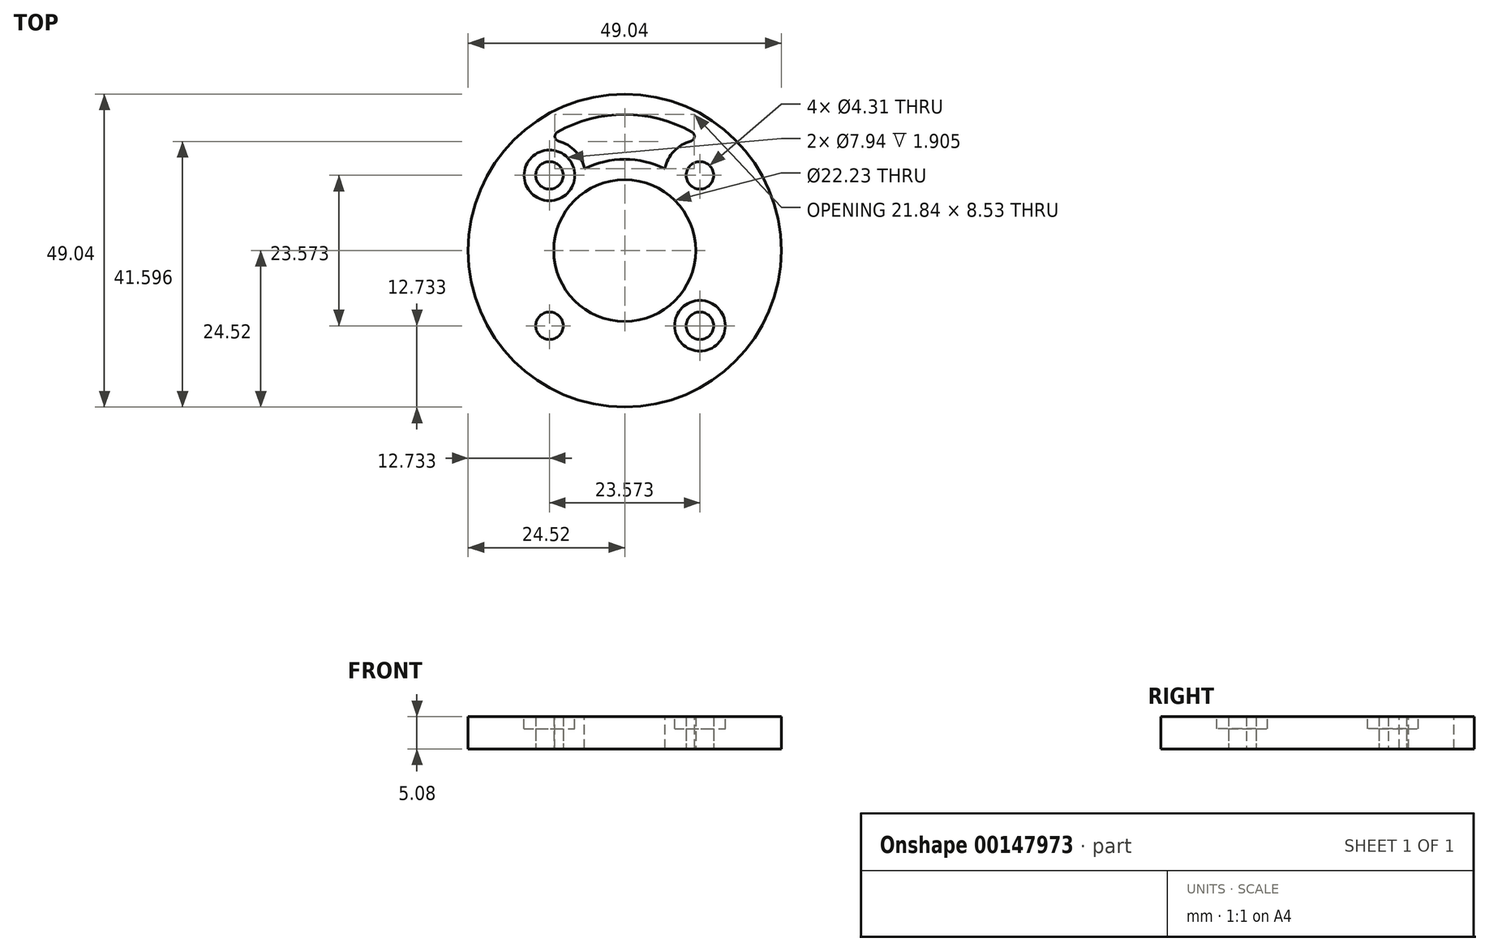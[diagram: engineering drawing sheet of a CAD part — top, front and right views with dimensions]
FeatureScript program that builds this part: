
annotation { "Feature Type Name" : "Feature", "Feature Type Description" : "" }
export const myFeature = defineFeature(function(context is Context, id is Id, definition is map)
    precondition{}
    {
        {
            var Q0;
            Q0=qCreatedBy(makeId("Top.planeOp"),FACE);
            var sketch = newSketch(context, id + "F0", { "sketchPlane" : qUnion([Q0])});
            skCircle(sketch, "E0", {"center": v(0, 0) * mm, "radius": 24.52 * mm});
            skCircle(sketch, "E1", {"center": v(0, 0) * mm, "radius": 11.11 * mm});
            skLineSegment(sketch, "E2.bottom", {"start": v(-11.79, 11.79) * mm, "end": v(11.79, 11.79) * mm, "construction": true});
            skLineSegment(sketch, "E2.top", {"start": v(-11.79, -11.79) * mm, "end": v(11.79, -11.79) * mm, "construction": true});
            skLineSegment(sketch, "E2.left", {"start": v(-11.79, 11.79) * mm, "end": v(-11.79, -11.79) * mm, "construction": true});
            skLineSegment(sketch, "E2.right", {"start": v(11.79, 11.79) * mm, "end": v(11.79, -11.79) * mm, "construction": true});
            skCircle(sketch, "E3", {"center": v(11.79, 11.79) * mm, "radius": 2.15 * mm});
            skCircle(sketch, "E4", {"center": v(-11.79, 11.79) * mm, "radius": 2.15 * mm});
            skCircle(sketch, "E5", {"center": v(-11.79, -11.79) * mm, "radius": 2.15 * mm});
            skCircle(sketch, "E6", {"center": v(11.79, -11.79) * mm, "radius": 2.15 * mm});
            skCircle(sketch, "E7", {"center": v(-11.79, -11.79) * mm, "radius": 3.97 * mm, "construction": true});
            skCircle(sketch, "E8", {"center": v(11.79, 11.79) * mm, "radius": 3.97 * mm, "construction": true});
            skSolve(sketch);
        }
        {
            var Q0;
            Q0=qSketchRegion(id+"F0",true);
            extrude(context, id + "F1", {"entities" : qUnion([Q0]), "depth" : 5.08 * mm});
        }
        {
            var Q0;
            Q0=makeQuery(id+"F1.opExtrude","CAP_FACE",FACE,{"disambiguationData":[OSD([sQuery(id+"F0.wireOp",EDGE,"E0"),sQuery(id+"F0.wireOp",EDGE,"E1"),sQuery(id+"F0.wireOp",EDGE,"E3"),sQuery(id+"F0.wireOp",EDGE,"E4"),sQuery(id+"F0.wireOp",EDGE,"E5"),sQuery(id+"F0.wireOp",EDGE,"E6")])],"isStart":false});
            var sketch = newSketch(context, id + "F2", { "sketchPlane" : qUnion([Q0])});
            skArc(sketch, "E9", {"start": v(-6.55, 9.92) * mm, "mid": v(-7.46, 15.27) * mm, "end": v(-12.5, 17.3) * mm});
            skArc(sketch, "E10", {"start": v(12.5, 17.3) * mm, "mid": v(7.46, 15.27) * mm, "end": v(6.55, 9.92) * mm});
            skArc(sketch, "E11", {"start": v(12.5, 17.3) * mm, "mid": v(0, 21.34) * mm, "end": v(-12.5, 17.3) * mm});
            skArc(sketch, "E12", {"start": v(8.28, 11.65) * mm, "mid": v(0, 14.29) * mm, "end": v(-8.28, 11.65) * mm});
            skLineSegment(sketch, "E13.bottom", {"start": v(-9.92, 6.55) * mm, "end": v(-6.55, 9.92) * mm, "construction": true});
            skLineSegment(sketch, "E13.top", {"start": v(-11.65, 8.28) * mm, "end": v(-8.28, 11.65) * mm, "construction": true});
            skLineSegment(sketch, "E13.left", {"start": v(-11.65, 8.28) * mm, "end": v(-9.92, 6.55) * mm, "construction": true});
            skLineSegment(sketch, "E13.right", {"start": v(-8.28, 11.65) * mm, "end": v(-6.55, 9.92) * mm});
            skLineSegment(sketch, "E14.bottom", {"start": v(9.92, 6.55) * mm, "end": v(6.55, 9.92) * mm, "construction": true});
            skLineSegment(sketch, "E14.top", {"start": v(11.65, 8.28) * mm, "end": v(8.28, 11.65) * mm, "construction": true});
            skLineSegment(sketch, "E14.left", {"start": v(11.65, 8.28) * mm, "end": v(9.92, 6.55) * mm, "construction": true});
            skLineSegment(sketch, "E14.right", {"start": v(8.28, 11.65) * mm, "end": v(6.55, 9.92) * mm});
            skLineSegment(sketch, "E15", {"start": v(-8.24, 8.24) * mm, "end": v(-11.79, 11.79) * mm, "construction": true});
            skLineSegment(sketch, "E16", {"start": v(-9.96, 9.96) * mm, "end": v(0, 0) * mm, "construction": true});
            skLineSegment(sketch, "E17", {"start": v(0, 0) * mm, "end": v(9.96, 9.96) * mm, "construction": true});
            skLineSegment(sketch, "E18", {"start": v(8.24, 8.24) * mm, "end": v(11.79, 11.79) * mm, "construction": true});
            skSolve(sketch);
        }
        {
            var Q0;
            Q0=makeQuery(id+"F2.imprint","IMPRINT",FACE,{"disambiguationData":[TD([[makeQuery(id+"F2.imprint","IMPRINT",EDGE,{"derivedFrom":sQuery(id+"F2.wireOp",EDGE,"E9")}),-1.0]])]});
            var Q1;
            Q1=makeQuery(id+"F1.opExtrude","CAP_FACE",FACE,{"disambiguationData":[OSD([sQuery(id+"F0.wireOp",EDGE,"E0"),sQuery(id+"F0.wireOp",EDGE,"E1"),sQuery(id+"F0.wireOp",EDGE,"E3"),sQuery(id+"F0.wireOp",EDGE,"E4"),sQuery(id+"F0.wireOp",EDGE,"E5"),sQuery(id+"F0.wireOp",EDGE,"E6")])],"isStart":true});
            extrude(context, id + "F3", {"entities" : qUnion([Q0]), "operationType" : NewBodyOperationType.REMOVE, "endBound" : BoundingType.UP_TO_SURFACE, "oppositeDirection" : true, "endBoundEntityFace" : qUnion([Q1]), "depth" : 25.4 * mm});
        }
        {
            var Q0;
            Q0=makeQuery(id+"F6MqURjXbY15YYN_1.1.F3.boolean.opBoolean","COPY",EDGE,{"derivedFrom":makeQuery(id+"F6MqURjXbY15YYN_1.1.F3.opExtrude","SWEPT_EDGE",EDGE,{"disambiguationData":[OSD([sQuery(id+"F2.wireOp",EDGE,"E9"),sQuery(id+"F2.wireOp",EDGE,"E11")])]})});
            var Q1;
            Q1=makeQuery(id+"F6MqURjXbY15YYN_1.1.F3.boolean.opBoolean","COPY",EDGE,{"derivedFrom":makeQuery(id+"F6MqURjXbY15YYN_1.1.F3.opExtrude","SWEPT_EDGE",EDGE,{"disambiguationData":[OSD([sQuery(id+"F2.wireOp",EDGE,"E10"),sQuery(id+"F2.wireOp",EDGE,"E11")])]})});
            var Q2;
            Q2=makeQuery(id+"F6MqURjXbY15YYN_1.2.F3.boolean.opBoolean","COPY",EDGE,{"derivedFrom":makeQuery(id+"F6MqURjXbY15YYN_1.2.F3.opExtrude","SWEPT_EDGE",EDGE,{"disambiguationData":[OSD([sQuery(id+"F2.wireOp",EDGE,"E9"),sQuery(id+"F2.wireOp",EDGE,"E11")])]})});
            var Q3;
            Q3=makeQuery(id+"F6MqURjXbY15YYN_1.2.F3.boolean.opBoolean","COPY",EDGE,{"derivedFrom":makeQuery(id+"F6MqURjXbY15YYN_1.2.F3.opExtrude","SWEPT_EDGE",EDGE,{"disambiguationData":[OSD([sQuery(id+"F2.wireOp",EDGE,"E10"),sQuery(id+"F2.wireOp",EDGE,"E11")])]})});
            var Q4;
            Q4=makeQuery(id+"F6MqURjXbY15YYN_1.3.F3.boolean.opBoolean","COPY",EDGE,{"derivedFrom":makeQuery(id+"F6MqURjXbY15YYN_1.3.F3.opExtrude","SWEPT_EDGE",EDGE,{"disambiguationData":[OSD([sQuery(id+"F2.wireOp",EDGE,"E9"),sQuery(id+"F2.wireOp",EDGE,"E11")])]})});
            var Q5;
            Q5=makeQuery(id+"F6MqURjXbY15YYN_1.3.F3.boolean.opBoolean","COPY",EDGE,{"derivedFrom":makeQuery(id+"F6MqURjXbY15YYN_1.3.F3.opExtrude","SWEPT_EDGE",EDGE,{"disambiguationData":[OSD([sQuery(id+"F2.wireOp",EDGE,"E10"),sQuery(id+"F2.wireOp",EDGE,"E11")])]})});
            var Q6;
            Q6=makeQuery(id+"F3.boolean.opBoolean","COPY",EDGE,{"derivedFrom":makeQuery(id+"F3.opExtrude","SWEPT_EDGE",EDGE,{"disambiguationData":[OSD([sQuery(id+"F2.wireOp",EDGE,"E9"),sQuery(id+"F2.wireOp",EDGE,"E11")])]})});
            var Q7;
            Q7=makeQuery(id+"F3.boolean.opBoolean","COPY",EDGE,{"derivedFrom":makeQuery(id+"F3.opExtrude","SWEPT_EDGE",EDGE,{"disambiguationData":[OSD([sQuery(id+"F2.wireOp",EDGE,"E10"),sQuery(id+"F2.wireOp",EDGE,"E11")])]})});
            fillet(context, id + "F4", {"entities" : qUnion([Q0, Q1, Q2, Q3, Q4, Q5, Q6, Q7]), "radius" : 0.76 * mm, "tangentPropagation" : true, "allowEdgeOverflow" : false});
        }
        {
            var Q0;
            Q0=makeQuery(id+"F1.opExtrude","CAP_FACE",FACE,{"disambiguationData":[OSD([sQuery(id+"F0.wireOp",EDGE,"E0"),sQuery(id+"F0.wireOp",EDGE,"E1"),sQuery(id+"F0.wireOp",EDGE,"E3"),sQuery(id+"F0.wireOp",EDGE,"E4"),sQuery(id+"F0.wireOp",EDGE,"E5"),sQuery(id+"F0.wireOp",EDGE,"E6")])],"isStart":true});
            cPlane(context, id + "F5", {"entities" : qUnion([Q0]), "cplaneType" : CPlaneType.OFFSET, "offset" : 3.17 * mm, "oppositeDirection" : true, "width" : 152.4 * mm, "height" : 152.4 * mm});
        }
        {
            var Q0;
            Q0=makeQuery(id+"F1.opExtrude","CAP_FACE",FACE,{"disambiguationData":[OSD([sQuery(id+"F0.wireOp",EDGE,"E0"),sQuery(id+"F0.wireOp",EDGE,"E1"),sQuery(id+"F0.wireOp",EDGE,"E3"),sQuery(id+"F0.wireOp",EDGE,"E4"),sQuery(id+"F0.wireOp",EDGE,"E5"),sQuery(id+"F0.wireOp",EDGE,"E6")])],"isStart":false});
            var sketch = newSketch(context, id + "F6", { "sketchPlane" : qUnion([Q0])});
            skCircle(sketch, "E19", {"center": v(11.79, -11.79) * mm, "radius": 3.97 * mm});
            skCircle(sketch, "E20", {"center": v(-11.79, 11.79) * mm, "radius": 3.97 * mm});
            skSolve(sketch);
        }
        {
            var Q0;
            Q0=qSketchRegion(id+"F6",true);
            var Q1;
            Q1=qCreatedBy(id+"F5.planeOp",FACE);
            extrude(context, id + "F7", {"entities" : qUnion([Q0]), "operationType" : NewBodyOperationType.REMOVE, "endBound" : BoundingType.UP_TO_SURFACE, "oppositeDirection" : true, "endBoundEntityFace" : qUnion([Q1]), "depth" : 25.4 * mm});
        }
    });
